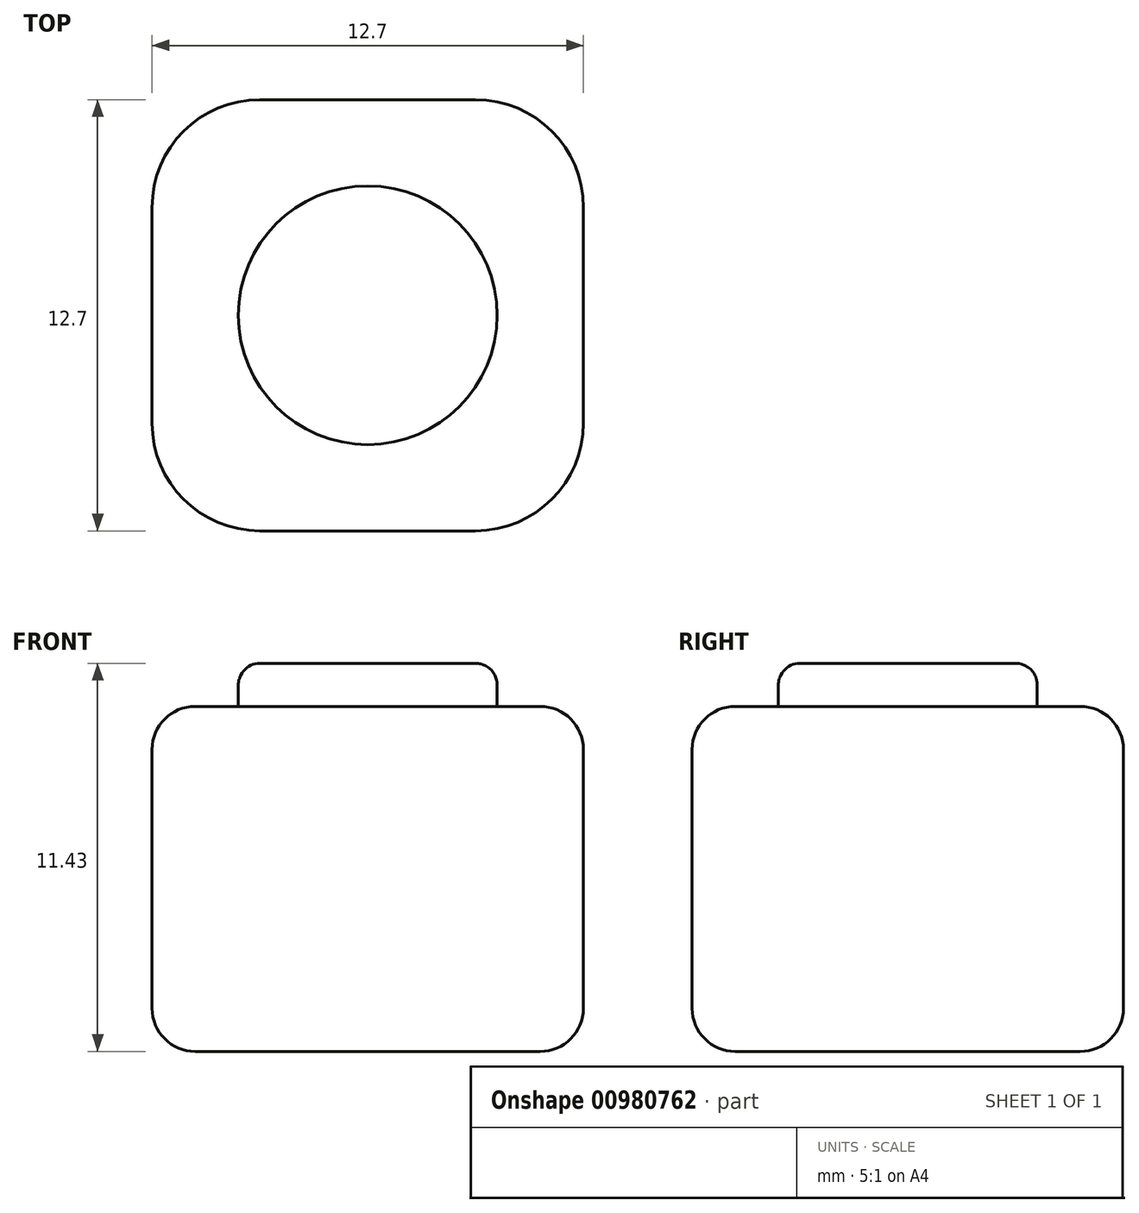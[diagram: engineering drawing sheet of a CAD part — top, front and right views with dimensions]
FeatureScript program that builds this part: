
annotation { "Feature Type Name" : "Feature", "Feature Type Description" : "" }
export const myFeature = defineFeature(function(context is Context, id is Id, definition is map)
    precondition{}
    {
        {
            var Q0;
            Q0=qCreatedBy(makeId("Top.planeOp"),FACE);
            var sketch = newSketch(context, id + "F0", { "sketchPlane" : qUnion([Q0])});
            skLineSegment(sketch, "E0.bottom", {"start": v(0, 0) * mm, "end": v(12.7, 0) * mm});
            skLineSegment(sketch, "E0.top", {"start": v(0, 12.7) * mm, "end": v(12.7, 12.7) * mm});
            skLineSegment(sketch, "E0.left", {"start": v(0, 0) * mm, "end": v(0, 12.7) * mm});
            skLineSegment(sketch, "E0.right", {"start": v(12.7, 0) * mm, "end": v(12.7, 12.7) * mm});
            skSolve(sketch);
        }
        {
            var Q0;
            Q0 = qSketchRegion(id + "F0", true);
            extrude(context, id + "F1", {"entities" : qUnion([Q0]), "depth" : 10.16 * mm, "offsetDistance" : 25.4 * mm});
        }
        {
            var Q0;
            Q0=makeQuery(id+"F1.opExtrude","SWEPT_EDGE",EDGE,{"disambiguationData":[OSD([sQuery(id+"F0.wireOp",EDGE,"E0.bottom"),sQuery(id+"F0.wireOp",EDGE,"E0.left")])]});
            var Q1;
            Q1=makeQuery(id+"F1.opExtrude","SWEPT_EDGE",EDGE,{"disambiguationData":[OSD([sQuery(id+"F0.wireOp",EDGE,"E0.bottom"),sQuery(id+"F0.wireOp",EDGE,"E0.right")])]});
            var Q2;
            Q2=makeQuery(id+"F1.opExtrude","SWEPT_EDGE",EDGE,{"disambiguationData":[OSD([sQuery(id+"F0.wireOp",EDGE,"E0.top"),sQuery(id+"F0.wireOp",EDGE,"E0.right")])]});
            var Q3;
            Q3=makeQuery(id+"F1.opExtrude","SWEPT_EDGE",EDGE,{"disambiguationData":[OSD([sQuery(id+"F0.wireOp",EDGE,"E0.top"),sQuery(id+"F0.wireOp",EDGE,"E0.left")])]});
            fillet(context, id + "F2", {"entities" : qUnion([Q0, Q1, Q2, Q3]), "radius" : 3.17 * mm, "tangentPropagation" : true, "allowEdgeOverflow" : false});
        }
        {
            var Q0;
            Q0=makeQuery(id+"F1.opExtrude","CAP_EDGE",EDGE,{"disambiguationData":[OSD([sQuery(id+"F0.wireOp",EDGE,"E0.bottom")])],"isStart":false});
            fillet(context, id + "F3", {"entities" : qUnion([Q0]), "radius" : 1.27 * mm, "tangentPropagation" : true, "allowEdgeOverflow" : false});
        }
        {
            var Q0;
            Q0=makeQuery(id+"F1.opExtrude","CAP_FACE",FACE,{"disambiguationData":[OSD([sQuery(id+"F0.wireOp",EDGE,"E0.bottom"),sQuery(id+"F0.wireOp",EDGE,"E0.top"),sQuery(id+"F0.wireOp",EDGE,"E0.left"),sQuery(id+"F0.wireOp",EDGE,"E0.right")])],"isStart":false});
            var sketch = newSketch(context, id + "F4", { "sketchPlane" : qUnion([Q0])});
            skCircle(sketch, "E1", {"center": v(6.35, 6.35) * mm, "radius": 3.81 * mm});
            skPoint(sketch, "E1.centerSnap0", {"position": v(1.27, 6.35) * mm});
            skSolve(sketch);
        }
        {
            var Q0;
            Q0 = qSketchRegion(id + "F4", true);
            extrude(context, id + "F5", {"entities" : qUnion([Q0]), "operationType" : NewBodyOperationType.ADD, "depth" : 1.27 * mm, "offsetDistance" : 25.4 * mm});
        }
        {
            var Q0;
            Q0=makeQuery(id+"F5.opExtrude","CAP_EDGE",EDGE,{"disambiguationData":[OSD([sQuery(id+"F4.wireOp",EDGE,"E1")])],"isStart":false});
            fillet(context, id + "F6", {"entities" : qUnion([Q0]), "radius" : 0.64 * mm, "tangentPropagation" : true, "allowEdgeOverflow" : false});
        }
        {
            var Q0;
            {var subQ0=sQuery(id+"F0.wireOp",EDGE,"E0.left");var subQ1=sQuery(id+"F0.wireOp",EDGE,"E0.bottom");Q0=makeQuery(id+"F2.opFillet","BLEND_EDGE",EDGE,{"blendedFrom":[makeQuery(id+"F1.opExtrude","SWEPT_EDGE",EDGE,{"disambiguationData":[OSD([subQ1,subQ0])]}),makeQuery(id+"F1.opExtrude","CAP_FACE",FACE,{"disambiguationData":[OSD([subQ1,sQuery(id+"F0.wireOp",EDGE,"E0.top"),subQ0,sQuery(id+"F0.wireOp",EDGE,"E0.right")])],"isStart":true})],"blendedInto":[makeQuery(id+"F1.opExtrude","CAP_FACE",FACE,{"disambiguationData":[OSD([subQ1,sQuery(id+"F0.wireOp",EDGE,"E0.top"),subQ0,sQuery(id+"F0.wireOp",EDGE,"E0.right")])],"isStart":true})]});}
            fillet(context, id + "F7", {"entities" : qUnion([Q0]), "radius" : 1.27 * mm, "tangentPropagation" : true, "allowEdgeOverflow" : false});
        }
    });
